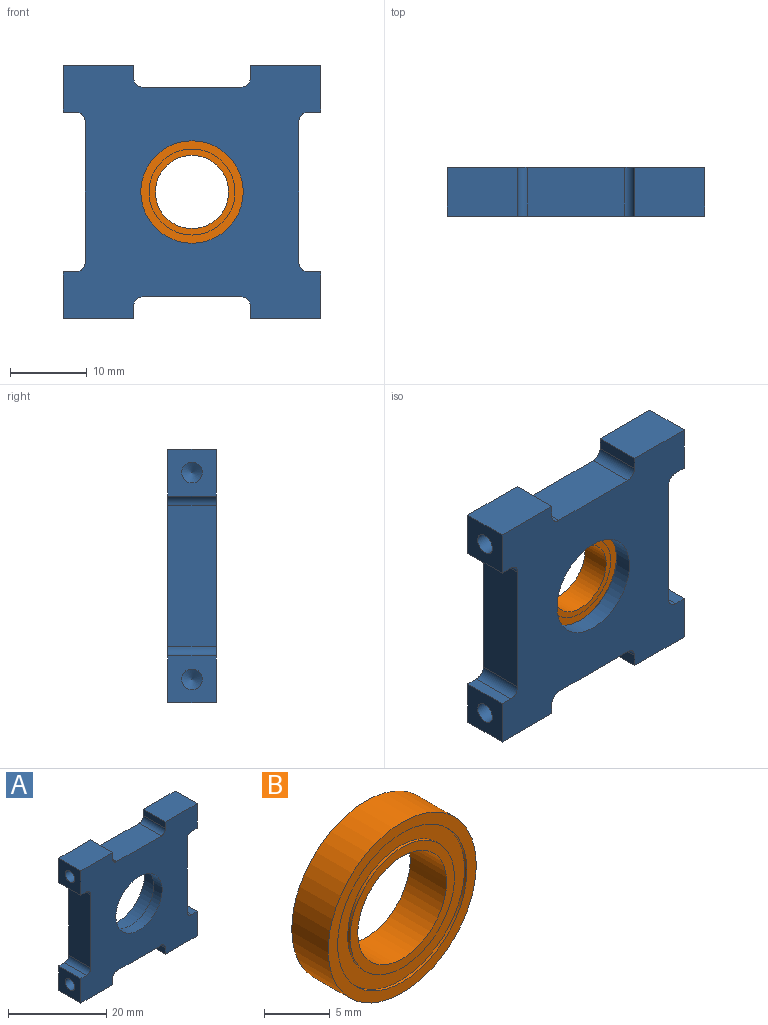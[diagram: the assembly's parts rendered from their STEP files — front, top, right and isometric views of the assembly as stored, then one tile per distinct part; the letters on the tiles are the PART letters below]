
ASSEMBLY  parts=2 mates=1
PART A: 41 faces, bbox 33.5x6.4x33 mm
  f0: cylinder r=6.67mm len=13.34mm, axis (0,1,0), area 100mm2, adj f31,f32
  f1: cylinder r=7.94mm len=15.88mm, axis (0,1,0), area 197.6mm2, adj f30,f32
  f2: cylinder r=1.35mm len=7.62mm, axis (1,0,0), area 64.8mm2, adj f3,f26
  f3: cone r=1.35mm half-angle=59deg, axis (1,0,0), area 6.7mm2, adj f2
  f4: cylinder r=1.35mm len=7.62mm, axis (1,0,0), area 64.8mm2, adj f5,f10
  f5: cone r=1.35mm half-angle=59deg, axis (1,0,0), area 6.7mm2, adj f4
  f6: cylinder r=1.35mm len=7.62mm, axis (-1,0,0), area 64.8mm2, adj f7,f20
  f7: cone r=1.35mm half-angle=59deg, axis (-1,0,0), area 6.7mm2, adj f6
  f8: cylinder r=1.35mm len=7.62mm, axis (-1,0,0), area 64.8mm2, adj f9,f16
  f9: cone r=1.35mm half-angle=59deg, axis (-1,0,0), area 6.7mm2, adj f8
  f10: plane 6.35x6.1mm, normal (1,0,0), area 33mm2, adj f4,f11,f29,f30,f31
  f11: plane 9.14x6.35mm, normal (0,0,-1), area 58.1mm2, adj f10,f12,f30,f31
  f12: plane 6.35x1.6mm, normal (-1,0,0), area 10.1mm2, adj f11,f30,f31,f39
  f13: plane 12.7x6.35mm, normal (0,0,-1), area 80.6mm2, adj f30,f31,f38,f39
  f14: plane 6.35x1.6mm, normal (1,0,0), area 10.1mm2, adj f15,f30,f31,f38
  f15: plane 9.14x6.35mm, normal (0,0,-1), area 58.1mm2, adj f14,f16,f30,f31
  f16: plane 6.35x6.1mm, normal (-1,0,0), area 33mm2, adj f8,f15,f17,f30,f31
  f17: plane 6.35x1.59mm, normal (0,0,1), area 10.1mm2, adj f16,f30,f31,f40
  f18: plane 18.29x6.35mm, normal (-1,0,0), area 116.1mm2, adj f30,f31,f37,f40
  f19: plane 6.35x1.59mm, normal (0,0,-1), area 10.1mm2, adj f20,f30,f31,f37
  f20: plane 6.35x6.1mm, normal (-1,0,0), area 33mm2, adj f6,f19,f21,f30,f31
  f21: plane 9.14x6.35mm, normal (0,0,1), area 58.1mm2, adj f20,f22,f30,f31
  f22: plane 6.35x1.6mm, normal (1,0,0), area 10.1mm2, adj f21,f30,f31,f36
  f23: plane 12.7x6.35mm, normal (0,0,1), area 80.6mm2, adj f30,f31,f35,f36
  f24: plane 6.35x1.6mm, normal (-1,0,0), area 10.1mm2, adj f25,f30,f31,f35
  f25: plane 9.14x6.35mm, normal (0,0,1), area 58.1mm2, adj f24,f26,f30,f31
  f26: plane 6.35x6.1mm, normal (1,0,0), area 33mm2, adj f2,f25,f27,f30,f31
  f27: plane 6.35x1.59mm, normal (0,0,-1), area 10.1mm2, adj f26,f30,f31,f34
  f28: plane 18.29x6.35mm, normal (1,0,0), area 116.1mm2, adj f30,f31,f33,f34
  f29: plane 6.35x1.59mm, normal (0,0,1), area 10.1mm2, adj f10,f30,f31,f33
  f30: plane 33.53x33.02mm, normal (0,1,0), area 705.6mm2, adj f1,f10,f11,f12,f13,f14,f15,f16
  f31: plane 33.53x33.02mm, normal (0,-1,0), area 763.8mm2, adj f0,f10,f11,f12,f13,f14,f15,f16
  f32: plane 15.88x15.88mm, normal (0,1,0), area 58.3mm2, adj f0,f1
  f33: cylinder r=1.27mm len=6.35mm, axis (0,1,0), area 12.7mm2, adj f28,f29,f30,f31
  f34: cylinder r=1.27mm len=6.35mm, axis (0,1,0), area 12.7mm2, adj f27,f28,f30,f31
  f35: cylinder r=1.27mm len=6.35mm, axis (0,1,0), area 12.7mm2, adj f23,f24,f30,f31
  f36: cylinder r=1.27mm len=6.35mm, axis (0,1,0), area 12.7mm2, adj f22,f23,f30,f31
  f37: cylinder r=1.27mm len=6.35mm, axis (0,1,0), area 12.7mm2, adj f18,f19,f30,f31
  f38: cylinder r=1.27mm len=6.35mm, axis (0,1,0), area 12.7mm2, adj f13,f14,f30,f31
  f39: cylinder r=1.27mm len=6.35mm, axis (0,1,0), area 12.7mm2, adj f12,f13,f30,f31
  f40: cylinder r=1.27mm len=6.35mm, axis (0,1,0), area 12.7mm2, adj f17,f18,f30,f31
PART B: 12 faces, bbox 15.9x3.9x15.9 mm
  f0: cylinder r=5.6mm len=11.2mm, axis (0,-1,0), area 8.9mm2, adj f6,f11
  f1: cylinder r=6.93mm len=13.87mm, axis (0,-1,0), area 11.1mm2, adj f9,f11
  f2: cylinder r=5.6mm len=11.2mm, axis (0,1,0), area 8.9mm2, adj f7,f10
  f3: cylinder r=6.93mm len=13.87mm, axis (0,1,0), area 11.1mm2, adj f8,f10
  f4: cylinder r=4.76mm len=9.53mm, axis (0,-1,0), area 117mm2, adj f6,f7
  f5: cylinder r=7.94mm len=15.88mm, axis (0,-1,0), area 195.1mm2, adj f8,f9
  f6: plane 11.2x11.2mm, normal (0,-1,0), area 27.3mm2, adj f0,f4
  f7: plane 11.2x11.2mm, normal (0,1,0), area 27.3mm2, adj f2,f4
  f8: plane 15.88x15.88mm, normal (0,1,0), area 46.9mm2, adj f3,f5
  f9: plane 15.88x15.88mm, normal (0,-1,0), area 46.9mm2, adj f1,f5
  f10: plane 13.87x13.87mm, normal (0,1,0), area 52.5mm2, adj f2,f3
  f11: plane 13.87x13.87mm, normal (0,-1,0), area 52.5mm2, adj f0,f1
PLACE A t=(10.13,14.09,27.15)mm
PLACE B t=(10.13,16.48,27.15)mm
MATE fastened B.f0 <-> A.f0  axis (0,-1,0) through (10.13,16.73,27.15)mm
